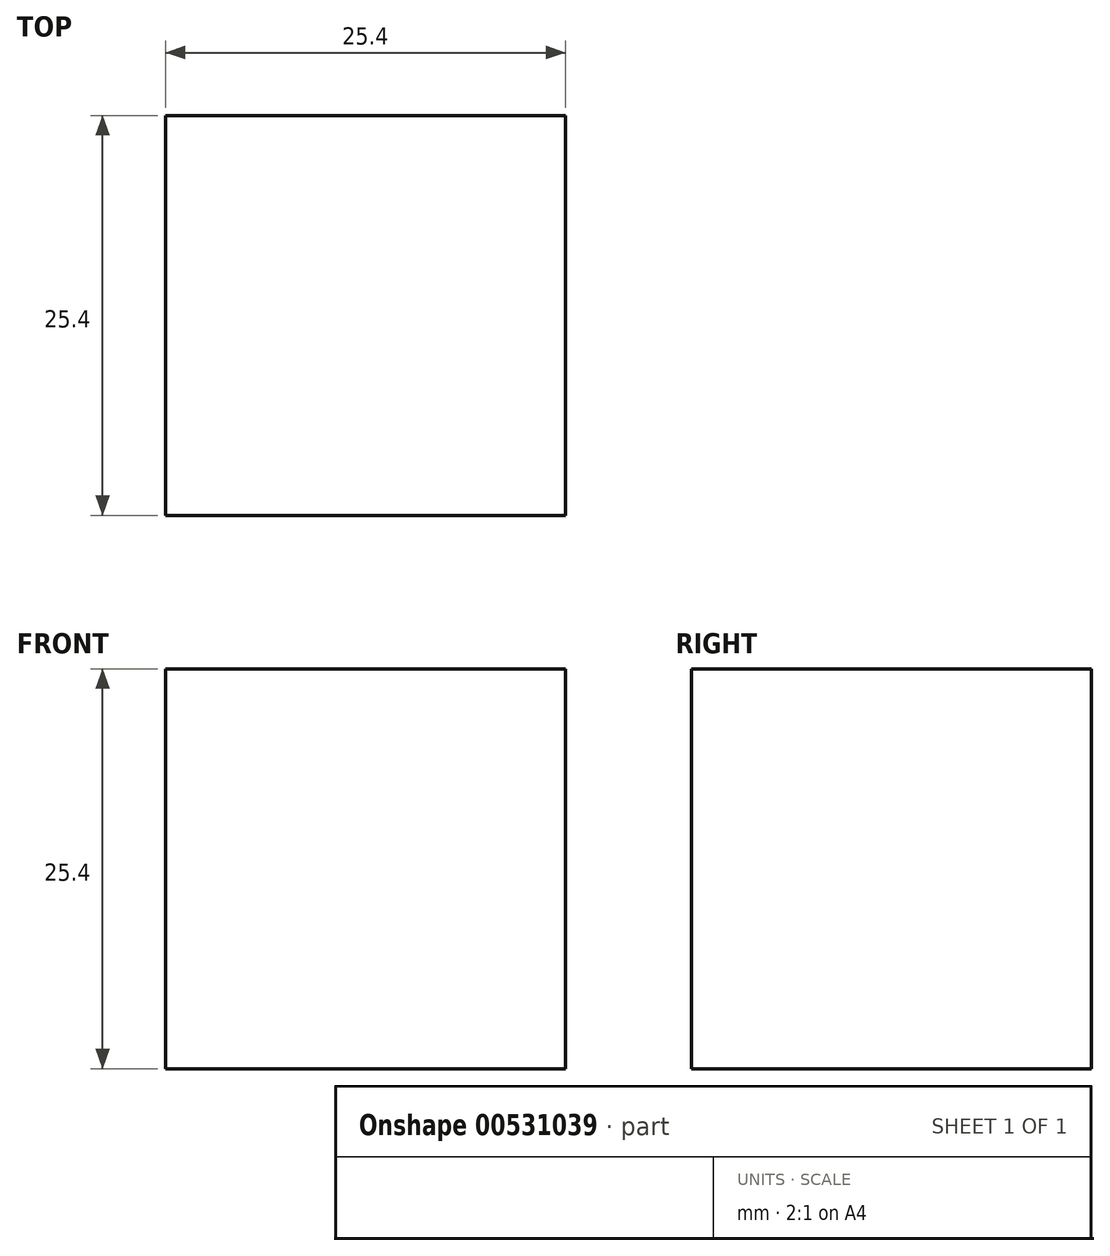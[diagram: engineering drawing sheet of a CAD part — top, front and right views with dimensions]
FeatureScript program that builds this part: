
annotation { "Feature Type Name" : "Feature", "Feature Type Description" : "" }
export const myFeature = defineFeature(function(context is Context, id is Id, definition is map)
    precondition{}
    {
        {
            var Q0;
            Q0=qCreatedBy(makeId("Front.planeOp"),FACE);
            var sketch = newSketch(context, id + "F0", { "sketchPlane" : qUnion([Q0])});
            skLineSegment(sketch, "E0", {"start": v(0, 0) * mm, "end": v(25.4, 0) * mm});
            skLineSegment(sketch, "E1", {"start": v(25.4, 0) * mm, "end": v(25.4, 25.4) * mm});
            skLineSegment(sketch, "E2", {"start": v(25.4, 25.4) * mm, "end": v(0, 25.4) * mm});
            skLineSegment(sketch, "E3", {"start": v(0, 25.4) * mm, "end": v(0, 0) * mm});
            skSolve(sketch);
        }
        {
            var Q0;
            Q0 = qSketchRegion(id + "F0", true);
            extrude(context, id + "F1", {"entities" : qUnion([Q0]), "depth" : 25.4 * mm, "offsetDistance" : 25.4 * mm});
        }
    });
